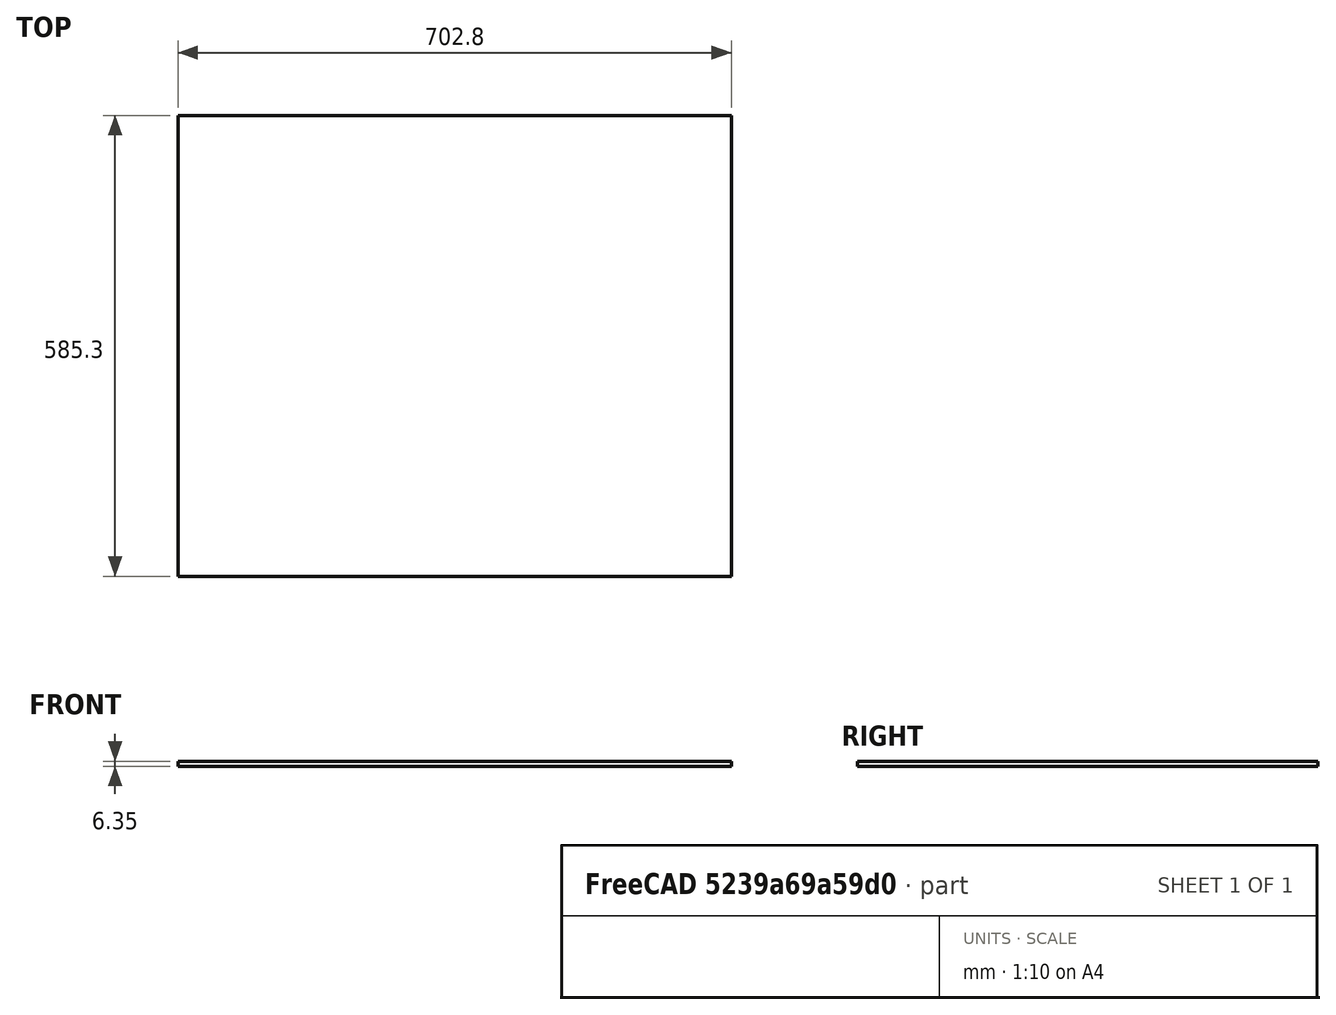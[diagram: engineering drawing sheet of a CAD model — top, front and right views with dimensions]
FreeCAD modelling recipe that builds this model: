
FCSTD DOCUMENT  (FreeCAD 0.19R24291 (Git))
Label: bottom2
License: All rights reserved
LicenseURL: http://en.wikipedia.org/wiki/All_rights_reserved
objects: Sketcher::SketchObject×1, PartDesign::Pad×1, PartDesign::Body×1
note: 4 computed .brp shape members not serialized (recipe doc carries the construction recipe); baked Part::Feature solids carry a one-line shape summary decoded from their .brp

FEATURE [Sketcher::SketchObject] Sketch
  FullyConstrained = true
  MapMode = 5
  Support = -> [XY_Plane]
  expr: Constraints[10] = 587.3 - 2
  expr: Constraints[9] = 704.8 - 2
  sketch-geometry (4):
    g0: LineSegment StartX=0 StartY=0 StartZ=0 EndX=702.8 EndY=0 EndZ=0
    g1: LineSegment StartX=702.8 StartY=0 StartZ=0 EndX=702.8 EndY=585.3 EndZ=0
    g2: LineSegment StartX=702.8 StartY=585.3 StartZ=0 EndX=0 EndY=585.3 EndZ=0
    g3: LineSegment StartX=0 StartY=585.3 StartZ=0 EndX=0 EndY=0 EndZ=0
  constraints (11):
    c: Coincident(g0,g1)
    c: Coincident(g1,g2)
    c: Coincident(g2,g3)
    c: Coincident(g3,g0)
    c: Horizontal(g0)
    c: Horizontal(g2)
    c: Vertical(g1)
    c: Vertical(g3)
    c: Coincident(g0,g-1)
    c: DistanceX(g0,g0) = 702.8
    c: DistanceY(g3,g3) = 585.3
FEATURE [PartDesign::Pad] Pad
  Direction = (1,1,1)
  Length = 6.35
  Length2 = 100
  Profile = -> Sketch
  Type = 0
  expr: Length = 1 / 4 * 25.4
FEATURE [PartDesign::Body] Body
  Group = -> [Sketch,Pad]
  Origin = -> Origin
  Tip = -> Pad
